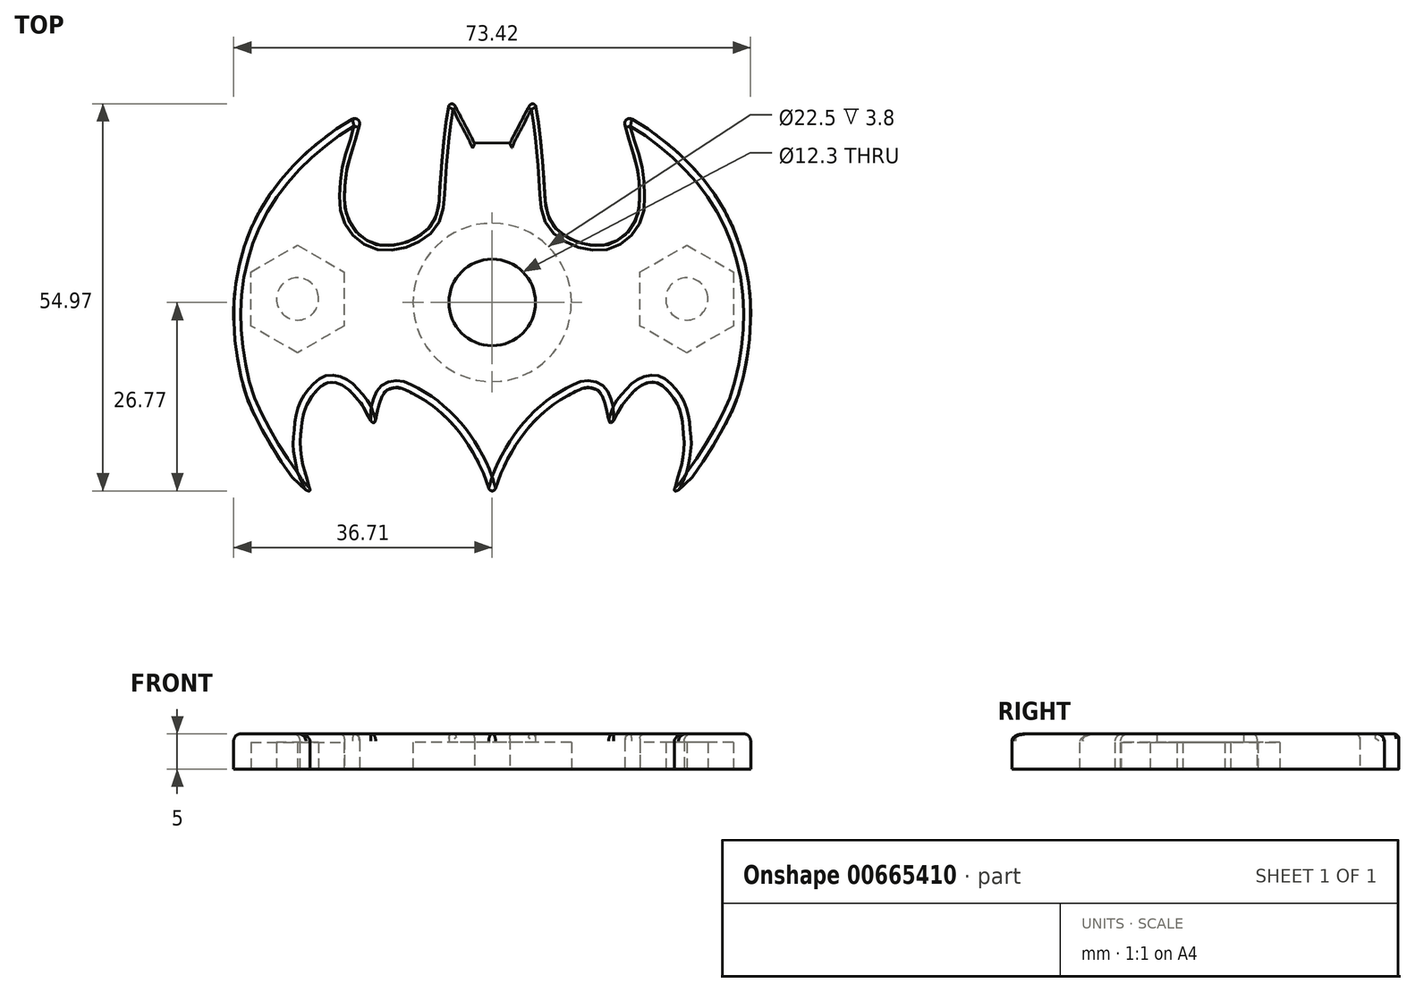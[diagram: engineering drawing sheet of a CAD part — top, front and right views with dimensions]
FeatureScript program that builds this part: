
annotation { "Feature Type Name" : "Feature", "Feature Type Description" : "" }
export const myFeature = defineFeature(function(context is Context, id is Id, definition is map)
    precondition{}
    {
        {
            var Q0;
            Q0=qCreatedBy(makeId("Top.planeOp"),FACE);
            var sketch = newSketch(context, id + "F0", { "sketchPlane" : qUnion([Q0])});
            skFitSpline(sketch, "E0", {"points": [v(0, -28.52) * mm, v(-1.27, -24.75) * mm, v(-4.07, -19.7) * mm, v(-6.91, -16.49) * mm, v(-9.48, -14.48) * mm, v(-12.37, -12.9) * mm, v(-13.4, -12.58) * mm, v(-14.24, -12.68) * mm, v(-15.05, -13.01) * mm, v(-15.53, -13.55) * mm, v(-15.82, -14.25) * mm, v(-16.3, -15.92) * mm, v(-16.85, -17.6) * mm, v(-18.3, -15.32) * mm, v(-19.18, -14.2) * mm, v(-20.02, -13.22) * mm, v(-21.19, -12.29) * mm, v(-22.54, -11.82) * mm, v(-23.75, -12.06) * mm, v(-25.06, -13.18) * mm, v(-26, -14.43) * mm, v(-26.55, -15.55) * mm, v(-26.97, -17.23) * mm, v(-27.11, -18.63) * mm, v(-27.25, -19.99) * mm, v(-27.2, -21.53) * mm, v(-26.97, -22.97) * mm, v(-26.74, -24.14) * mm, v(-26.27, -25.63) * mm, v(-26, -26.7) * mm, v(-25.9, -27.22) * mm, v(-27.11, -26.7) * mm, v(-33.04, -17.89) * mm, v(-35.46, -11.92) * mm, v(-36.68, -0.49) * mm, v(-34.06, 10.38) * mm, v(-30.1, 16.82) * mm, v(-25.8, 21.25) * mm, v(-22.38, 23.95) * mm, v(-20.53, 25.17) * mm, v(-18.53, 26.06) * mm], "startDerivative": vector(-32.32, 112.77) * mm, "endDerivative": vector(75.75, 17.62) * mm});
            skFitSpline(sketch, "E1", {"points": [v(-18.53, 26.06) * mm, v(-19.44, 22.57) * mm, v(-20.66, 18.35) * mm, v(-20.96, 14.62) * mm, v(-20.66, 11.88) * mm, v(-19.17, 9.37) * mm, v(-18.05, 8.52) * mm, v(-16.57, 7.76) * mm, v(-13.86, 7.66) * mm, v(-11.36, 8.38) * mm, v(-10.1, 9.14) * mm, v(-8.95, 10.1) * mm, v(-7.76, 12.34) * mm, v(-7.46, 15.08) * mm, v(-7.2, 18.87) * mm, v(-6.57, 25.1) * mm, v(-5.95, 28.67) * mm], "startDerivative": vector(-11.5, -48.57) * mm, "endDerivative": vector(9.26, 45.89) * mm});
            skFitSpline(sketch, "E2", {"points": [v(-5.95, 28.67) * mm, v(-2.55, 22.17) * mm, v(-2.54, 22.14) * mm], "startDerivative": vector(5.32, -9.94) * mm, "endDerivative": vector(0.15, -0.33) * mm});
            skFitSpline(sketch, "E3.MirrorCS", {"points": [v(5.95, 28.67) * mm, v(2.55, 22.17) * mm, v(2.54, 22.15) * mm], "startDerivative": vector(-5.32, -9.94) * mm, "endDerivative": vector(-0.13, -0.34) * mm});
            skFitSpline(sketch, "E4.MirrorCS", {"points": [v(0, -28.52) * mm, v(1.27, -24.75) * mm, v(4.07, -19.7) * mm, v(6.91, -16.49) * mm, v(9.48, -14.48) * mm, v(12.37, -12.9) * mm, v(13.4, -12.58) * mm, v(14.24, -12.68) * mm, v(15.05, -13.01) * mm, v(15.53, -13.55) * mm, v(15.82, -14.25) * mm, v(16.3, -15.92) * mm, v(16.85, -17.6) * mm, v(18.3, -15.32) * mm, v(19.18, -14.2) * mm, v(20.02, -13.22) * mm, v(21.19, -12.29) * mm, v(22.54, -11.82) * mm, v(23.75, -12.06) * mm, v(25.06, -13.18) * mm, v(26, -14.43) * mm, v(26.55, -15.55) * mm, v(26.97, -17.23) * mm, v(27.11, -18.63) * mm, v(27.25, -19.99) * mm, v(27.2, -21.53) * mm, v(26.97, -22.97) * mm, v(26.74, -24.14) * mm, v(26.27, -25.63) * mm, v(26, -26.7) * mm, v(25.9, -27.22) * mm, v(27.11, -26.7) * mm, v(33.04, -17.89) * mm, v(35.46, -11.92) * mm, v(36.68, -0.49) * mm, v(34.06, 10.38) * mm, v(30.1, 16.82) * mm, v(25.8, 21.25) * mm, v(22.38, 23.95) * mm, v(20.53, 25.17) * mm, v(18.53, 26.06) * mm], "startDerivative": vector(32.32, 112.77) * mm, "endDerivative": vector(-75.75, 17.62) * mm});
            skFitSpline(sketch, "E5.MirrorCS", {"points": [v(18.53, 26.06) * mm, v(19.44, 22.57) * mm, v(20.66, 18.35) * mm, v(20.96, 14.62) * mm, v(20.66, 11.88) * mm, v(19.17, 9.37) * mm, v(18.05, 8.52) * mm, v(16.57, 7.76) * mm, v(13.86, 7.66) * mm, v(11.36, 8.38) * mm, v(10.1, 9.14) * mm, v(8.95, 10.1) * mm, v(7.76, 12.34) * mm, v(7.46, 15.08) * mm, v(7.2, 18.87) * mm, v(6.57, 25.1) * mm, v(5.95, 28.67) * mm], "startDerivative": vector(11.5, -48.57) * mm, "endDerivative": vector(-9.26, 45.89) * mm});
            skLineSegment(sketch, "E6", {"start": v(-2.54, 22.14) * mm, "end": v(2.54, 22.15) * mm});
            skSolve(sketch);
        }
        {
            var Q0;
            Q0=qCreatedBy(makeId("Top.planeOp"),FACE);
            var sketch = newSketch(context, id + "F1", { "sketchPlane" : qUnion([Q0])});
            skLineSegment(sketch, "E7", {"start": v(0, 0) * mm, "end": v(0, -0.5) * mm});
            skCircle(sketch, "E8", {"center": v(0, -0.5) * mm, "radius": 11.25 * mm});
            skLineSegment(sketch, "E9.bottom", {"start": v(27.64, -1) * mm, "end": v(-27.64, -1) * mm, "construction": true});
            skLineSegment(sketch, "E9.top", {"start": v(27.64, 0) * mm, "end": v(-27.64, 0) * mm, "construction": true});
            skLineSegment(sketch, "E9.left", {"start": v(27.64, -1) * mm, "end": v(27.64, 0) * mm, "construction": true});
            skLineSegment(sketch, "E9.right", {"start": v(-27.64, -1) * mm, "end": v(-27.64, 0) * mm, "construction": true});
            skLineSegment(sketch, "E10.bottom", {"start": v(30.53, -10.33) * mm, "end": v(-30.53, -10.33) * mm, "construction": true});
            skLineSegment(sketch, "E10.top", {"start": v(30.53, 9.33) * mm, "end": v(-30.53, 9.33) * mm, "construction": true});
            skLineSegment(sketch, "E10.left", {"start": v(30.53, -10.33) * mm, "end": v(30.53, 9.33) * mm, "construction": true});
            skLineSegment(sketch, "E10.right", {"start": v(-30.53, -10.33) * mm, "end": v(-30.53, 9.33) * mm, "construction": true});
            skCircle(sketch, "E11", {"center": v(0, -0.5) * mm, "radius": 6.15 * mm});
            skCircle(sketch, "E12.cCircle", {"center": v(-27.64, 0) * mm, "radius": 6.63 * mm, "construction": true});
            skLineSegment(sketch, "E12.0", {"start": v(-21.02, 3.82) * mm, "end": v(-21.02, -3.82) * mm});
            skLineSegment(sketch, "E12.1", {"start": v(-21.02, -3.82) * mm, "end": v(-27.64, -7.65) * mm});
            skLineSegment(sketch, "E12.2", {"start": v(-27.64, -7.65) * mm, "end": v(-34.27, -3.82) * mm});
            skLineSegment(sketch, "E12.3", {"start": v(-34.27, -3.82) * mm, "end": v(-34.27, 3.82) * mm});
            skLineSegment(sketch, "E12.4", {"start": v(-34.27, 3.82) * mm, "end": v(-27.64, 7.65) * mm});
            skLineSegment(sketch, "E12.5", {"start": v(-27.64, 7.65) * mm, "end": v(-21.02, 3.82) * mm});
            skPoint(sketch, "E12.0.midPoint", {"position": v(-21.02, 0) * mm});
            skCircle(sketch, "E13.cCircle", {"center": v(27.64, 0) * mm, "radius": 6.62 * mm, "construction": true});
            skLineSegment(sketch, "E13.0", {"start": v(21.02, -3.82) * mm, "end": v(21.02, 3.82) * mm});
            skLineSegment(sketch, "E13.1", {"start": v(21.02, 3.82) * mm, "end": v(27.64, 7.65) * mm});
            skLineSegment(sketch, "E13.2", {"start": v(27.64, 7.65) * mm, "end": v(34.27, 3.82) * mm});
            skLineSegment(sketch, "E13.3", {"start": v(34.27, 3.82) * mm, "end": v(34.27, -3.82) * mm});
            skLineSegment(sketch, "E13.4", {"start": v(34.27, -3.82) * mm, "end": v(27.64, -7.65) * mm});
            skLineSegment(sketch, "E13.5", {"start": v(27.64, -7.65) * mm, "end": v(21.02, -3.82) * mm});
            skPoint(sketch, "E13.0.midPoint", {"position": v(21.02, 0) * mm});
            skCircle(sketch, "E14", {"center": v(-27.64, 0) * mm, "radius": 3 * mm});
            skCircle(sketch, "E15", {"center": v(27.64, 0) * mm, "radius": 3 * mm});
            skSolve(sketch);
        }
        {
            var Q0;
            Q0 = qSketchRegion(id + "F0", true);
            extrude(context, id + "F2", {"entities" : qUnion([Q0]), "depth" : 5 * mm, "offsetDistance" : 25 * mm});
        }
        {
            var Q0;
            Q0=makeQuery(id+"F1.imprint","IMPRINT",FACE,{"disambiguationData":[TD([[makeQuery(id+"F1.imprint","IMPRINT",EDGE,{"derivedFrom":sQuery(id+"F1.wireOp",EDGE,"E12.0")}),-1.0]])]});
            var Q1;
            Q1=makeQuery(id+"F1.imprint","IMPRINT",FACE,{"disambiguationData":[TD([[makeQuery(id+"F1.imprint","IMPRINT",EDGE,{"derivedFrom":sQuery(id+"F1.wireOp",EDGE,"E8")}),1.0]])]});
            var Q2;
            Q2=makeQuery(id+"F1.imprint","IMPRINT",FACE,{"disambiguationData":[TD([[makeQuery(id+"F1.imprint","IMPRINT",EDGE,{"derivedFrom":sQuery(id+"F1.wireOp",EDGE,"E13.0")}),-1.0]])]});
            extrude(context, id + "F3", {"entities" : qUnion([Q0, Q1, Q2]), "operationType" : NewBodyOperationType.REMOVE, "depth" : 3.8 * mm, "offsetDistance" : 25 * mm});
        }
        {
            var Q0;
            Q0=makeQuery(id+"F1.imprint","IMPRINT",FACE,{"disambiguationData":[TD([[makeQuery(id+"F1.imprint","IMPRINT",EDGE,{"derivedFrom":sQuery(id+"F1.wireOp",EDGE,"E11")}),1.0]])]});
            extrude(context, id + "F4", {"entities" : qUnion([Q0]), "operationType" : NewBodyOperationType.REMOVE, "depth" : 5 * mm, "offsetDistance" : 25 * mm});
        }
        {
            var Q0;
            Q0=makeQuery(id+"F2.opExtrude","CAP_EDGE",EDGE,{"disambiguationData":[OSD([sQuery(id+"F0.wireOp",EDGE,"E4.MirrorCS")])],"isStart":false});
            var Q1;
            Q1=makeQuery(id+"F2.opExtrude","CAP_EDGE",EDGE,{"disambiguationData":[OSD([sQuery(id+"F0.wireOp",EDGE,"E0")])],"isStart":false});
            fillet(context, id + "F5", {"entities" : qUnion([Q0, Q1]), "radius" : 1 * mm, "tangentPropagation" : true, "allowEdgeOverflow" : false});
        }
        {
            var Q0;
            Q0=makeQuery(id+"F2.opExtrude","CAP_EDGE",EDGE,{"disambiguationData":[OSD([sQuery(id+"F0.wireOp",EDGE,"E1")])],"isStart":false});
            var Q1;
            Q1=makeQuery(id+"F2.opExtrude","CAP_EDGE",EDGE,{"disambiguationData":[OSD([sQuery(id+"F0.wireOp",EDGE,"E5.MirrorCS")])],"isStart":false});
            var Q2;
            Q2=makeQuery(id+"F2.opExtrude","CAP_EDGE",EDGE,{"disambiguationData":[OSD([sQuery(id+"F0.wireOp",EDGE,"E6")])],"isStart":false});
            fillet(context, id + "F6", {"entities" : qUnion([Q0, Q1, Q2]), "radius" : .7 * mm, "tangentPropagation" : true, "allowEdgeOverflow" : false});
        }
        {
            var Q0;
            Q0=makeQuery(id+"F2.opExtrude","CAP_EDGE",EDGE,{"disambiguationData":[OSD([sQuery(id+"F0.wireOp",EDGE,"E2")])],"isStart":false});
            var Q1;
            Q1=makeQuery(id+"F2.opExtrude","SWEPT_EDGE",EDGE,{"disambiguationData":[OSD([sQuery(id+"F0.wireOp",EDGE,"E1"),sQuery(id+"F0.wireOp",EDGE,"E2")])]});
            var Q2;
            Q2=makeQuery(id+"F2.opExtrude","SWEPT_EDGE",EDGE,{"disambiguationData":[OSD([sQuery(id+"F0.wireOp",EDGE,"E3.MirrorCS"),sQuery(id+"F0.wireOp",EDGE,"E5.MirrorCS")])]});
            var Q3;
            Q3=makeQuery(id+"F2.opExtrude","CAP_EDGE",EDGE,{"disambiguationData":[OSD([sQuery(id+"F0.wireOp",EDGE,"E3.MirrorCS")])],"isStart":false});
            var Q4;
            Q4=makeQuery(id+"F2.opExtrude","SWEPT_EDGE",EDGE,{"disambiguationData":[OSD([sQuery(id+"F0.wireOp",EDGE,"E0"),sQuery(id+"F0.wireOp",EDGE,"E4.MirrorCS")])]});
            fillet(context, id + "F7", {"entities" : qUnion([Q0, Q1, Q2, Q3, Q4]), "radius" : .5 * mm, "tangentPropagation" : true, "allowEdgeOverflow" : false});
        }
    });
